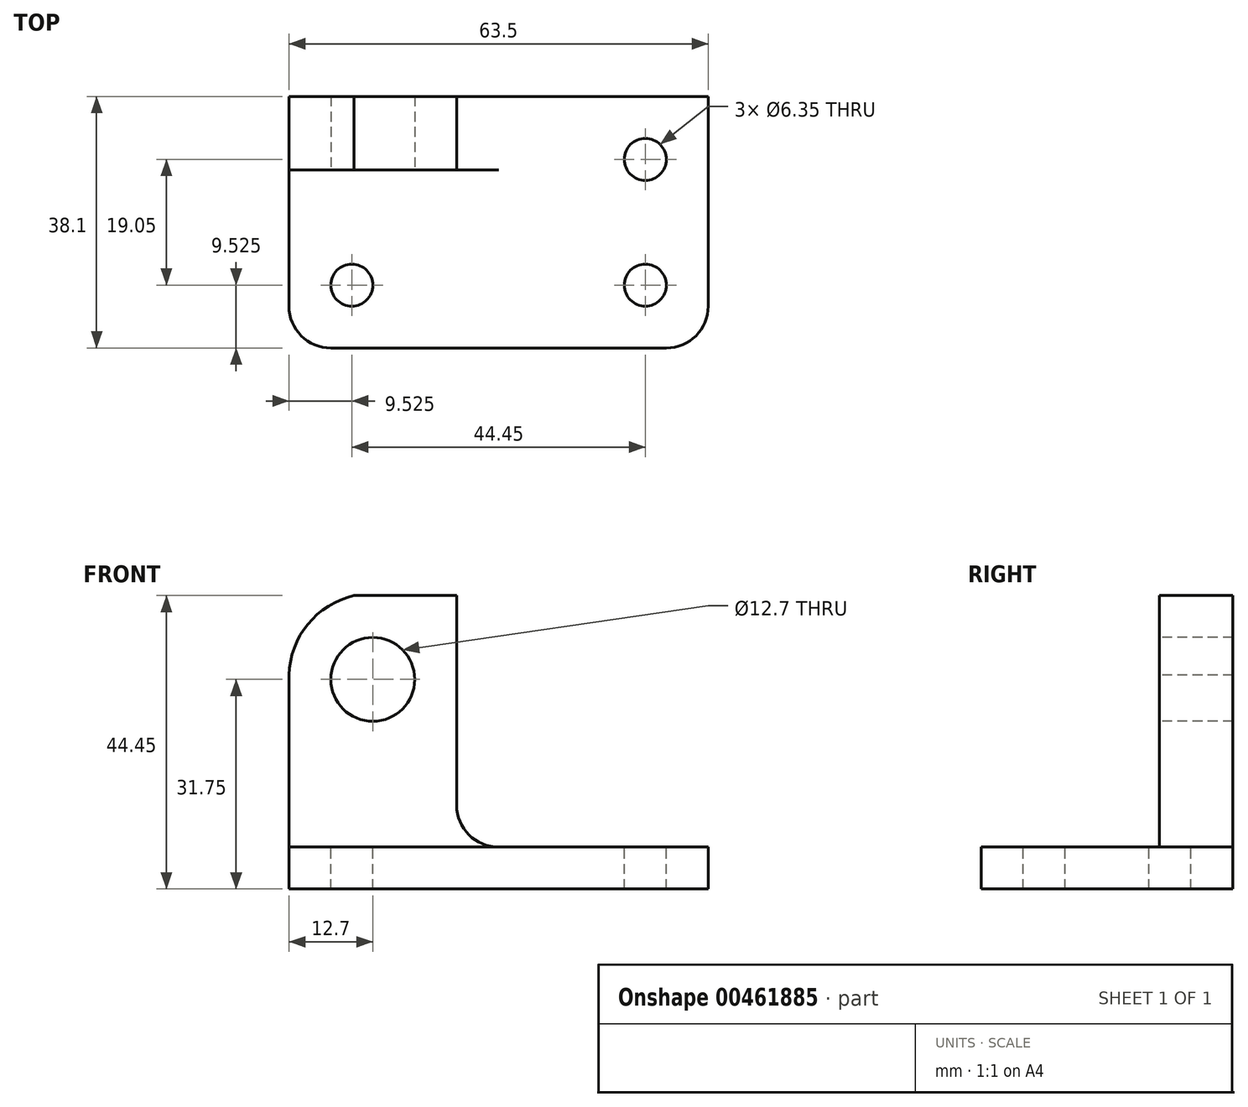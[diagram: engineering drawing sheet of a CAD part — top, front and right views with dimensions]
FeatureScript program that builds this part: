
annotation { "Feature Type Name" : "Feature", "Feature Type Description" : "" }
export const myFeature = defineFeature(function(context is Context, id is Id, definition is map)
    precondition{}
    {
        {
            var Q0;
            Q0=qCreatedBy(makeId("Right.planeOp"),FACE);
            var sketch = newSketch(context, id + "F0", { "sketchPlane" : qUnion([Q0])});
            skLineSegment(sketch, "E0", {"start": v(0, 0) * mm, "end": v(38.1, 0) * mm});
            skLineSegment(sketch, "E1", {"start": v(38.1, 0) * mm, "end": v(38.1, 44.45) * mm});
            skLineSegment(sketch, "E2", {"start": v(38.1, 44.45) * mm, "end": v(26.96, 44.45) * mm});
            skLineSegment(sketch, "E3", {"start": v(26.96, 44.45) * mm, "end": v(26.96, 6.35) * mm});
            skLineSegment(sketch, "E4", {"start": v(26.96, 6.35) * mm, "end": v(0, 6.35) * mm});
            skLineSegment(sketch, "E5", {"start": v(0, 6.35) * mm, "end": v(0, 0) * mm});
            skSolve(sketch);
        }
        {
            var Q0;
            Q0=makeQuery(id+"F0.imprint","IMPRINT",FACE,{"disambiguationData":[TD([[makeQuery(id+"F0.imprint","IMPRINT",EDGE,{"derivedFrom":sQuery(id+"F0.wireOp",EDGE,"E0")}),1.0]])]});
            extrude(context, id + "F1", {"entities" : qUnion([Q0]), "depth" : 63.5 * mm});
        }
        {
            var Q0;
            Q0=makeQuery(id+"F1.opExtrude","SWEPT_FACE",FACE,{"disambiguationData":[OSD([sQuery(id+"F0.wireOp",EDGE,"E3")])]});
            var sketch = newSketch(context, id + "F2", { "sketchPlane" : qUnion([Q0])});
            skLineSegment(sketch, "E6", {"start": v(25.4, 44.45) * mm, "end": v(25.4, 12.7) * mm});
            skLineSegment(sketch, "E7", {"start": v(31.75, 6.35) * mm, "end": v(63.5, 6.35) * mm});
            skPoint(sketch, "E8.visualSharp", {"position": v(25.4, 6.35) * mm});
            skArc(sketch, "E8.filletArc", {"start": v(25.4, 12.7) * mm, "mid": v(27.26, 8.2) * mm, "end": v(31.75, 6.35) * mm});
            skSolve(sketch);
        }
        {
            var Q0;
            {var subQ2=sQuery(id+"F2.wireOp",EDGE,"E6");Q0=makeQuery(id+"F2.imprint","IMPRINT",FACE,{"disambiguationData":[TD([[makeQuery(id+"F2.imprint","IMPRINT",EDGE,{"derivedFrom":subQ2}),1.0]])]});}
            extrude(context, id + "F3", {"entities" : qUnion([Q0]), "operationType" : NewBodyOperationType.REMOVE, "oppositeDirection" : true, "depth" : 12.7 * mm});
        }
        {
            var Q0;
            Q0=makeQuery(id+"F1.opExtrude","SWEPT_FACE",FACE,{"disambiguationData":[OSD([sQuery(id+"F0.wireOp",EDGE,"E3")])]});
            var sketch = newSketch(context, id + "F4", { "sketchPlane" : qUnion([Q0])});
            skCircle(sketch, "E9", {"center": v(12.7, 31.75) * mm, "radius": 6.35 * mm});
            skArc(sketch, "E10", {"start": v(25.4, 31.75) * mm, "mid": v(12.7, 44.77) * mm, "end": v(0, 31.75) * mm});
            skSolve(sketch);
        }
        {
            var Q0;
            {var subQ0=sQuery(id+"F4.wireOp",EDGE,"E10");var subQ1=makeQuery(id+"F3.boolean.opBoolean","COPY",EDGE,{"derivedFrom":makeQuery(id+"F3.opExtrude","CAP_EDGE",EDGE,{"disambiguationData":[OSD([sQuery(id+"F2.wireOp",EDGE,"E6")])],"isStart":true})});var subQ2=makeQuery(id+"F4.imprint","INTERSECT",VERTEX,{"disambiguationData":[OD(1.0)],"derivedFrom":[subQ1,subQ0]});Q0=makeQuery(id+"F4.imprint","IMPRINT",FACE,{"disambiguationData":[TD([[makeQuery(id+"F4.imprint","IMPRINT",EDGE,{"disambiguationData":[TD([[subQ2,-1.0]])],"derivedFrom":subQ0}),-1.0]])]});}
            var Q1;
            Q1=makeQuery(id+"F4.imprint","IMPRINT",FACE,{"disambiguationData":[TD([[makeQuery(id+"F4.imprint","IMPRINT",EDGE,{"derivedFrom":sQuery(id+"F4.wireOp",EDGE,"E9")}),1.0]])]});
            var Q2;
            {var subQ0=sQuery(id+"F4.wireOp",EDGE,"E10");var subQ1=sQuery(id+"F0.wireOp",EDGE,"E3");var subQ4=makeQuery(id+"F1.opExtrude","CAP_EDGE",EDGE,{"disambiguationData":[OSD([subQ1])],"isStart":true});var subQ5=makeQuery(id+"F4.imprint","INTERSECT",VERTEX,{"disambiguationData":[OD(1.0)],"derivedFrom":[subQ4,subQ0]});Q2=makeQuery(id+"F4.imprint","IMPRINT",FACE,{"disambiguationData":[TD([[makeQuery(id+"F4.imprint","IMPRINT",EDGE,{"disambiguationData":[TD([[subQ5,1.0]])],"derivedFrom":subQ0}),-1.0]])]});}
            extrude(context, id + "F5", {"entities" : qUnion([Q0, Q1, Q2]), "operationType" : NewBodyOperationType.REMOVE, "oppositeDirection" : true, "depth" : 12.7 * mm});
        }
        {
            var Q0;
            Q0=makeQuery(id+"F3.boolean.opBoolean","MERGE",FACE,{"derivedFrom":[makeQuery(id+"F1.opExtrude","SWEPT_FACE",FACE,{"disambiguationData":[OSD([sQuery(id+"F0.wireOp",EDGE,"E4")])]}),makeQuery(id+"F3.opExtrude","SWEPT_FACE",FACE,{"disambiguationData":[OSD([sQuery(id+"F2.wireOp",EDGE,"E7")])]})]});
            var sketch = newSketch(context, id + "F6", { "sketchPlane" : qUnion([Q0])});
            skCircle(sketch, "E11", {"center": v(53.98, 9.53) * mm, "radius": 3.18 * mm});
            skCircle(sketch, "E12", {"center": v(9.53, 9.53) * mm, "radius": 3.17 * mm});
            skCircle(sketch, "E13", {"center": v(53.97, 28.58) * mm, "radius": 3.18 * mm});
            skLineSegment(sketch, "E14", {"start": v(0, 26.96) * mm, "end": v(0, 6.35) * mm});
            skLineSegment(sketch, "E15", {"start": v(6.35, 0) * mm, "end": v(57.15, 0) * mm});
            skPoint(sketch, "E16.visualSharp", {"position": v(0, 0) * mm});
            skArc(sketch, "E16.filletArc", {"start": v(0, 6.35) * mm, "mid": v(1.86, 1.86) * mm, "end": v(6.35, 0) * mm});
            skLineSegment(sketch, "E17", {"start": v(63.5, 6.35) * mm, "end": v(63.5, 38.1) * mm});
            skPoint(sketch, "E18.visualSharp", {"position": v(63.5, 0) * mm});
            skArc(sketch, "E18.filletArc", {"start": v(57.15, 0) * mm, "mid": v(61.64, 1.86) * mm, "end": v(63.5, 6.35) * mm});
            skSolve(sketch);
        }
        {
            var Q0;
            Q0=makeQuery(id+"F6.imprint","IMPRINT",FACE,{"disambiguationData":[TD([[makeQuery(id+"F6.imprint","IMPRINT",EDGE,{"derivedFrom":sQuery(id+"F6.wireOp",EDGE,"E11")}),1.0]])]});
            var Q1;
            {var subQ0=sQuery(id+"F6.wireOp",EDGE,"E18.filletArc");Q1=makeQuery(id+"F6.imprint","IMPRINT",FACE,{"disambiguationData":[TD([[makeQuery(id+"F6.imprint","IMPRINT",EDGE,{"derivedFrom":subQ0}),-1.0]])]});}
            var Q2;
            {var subQ0=sQuery(id+"F6.wireOp",EDGE,"E16.filletArc");Q2=makeQuery(id+"F6.imprint","IMPRINT",FACE,{"disambiguationData":[TD([[makeQuery(id+"F6.imprint","IMPRINT",EDGE,{"derivedFrom":subQ0}),-1.0]])]});}
            var Q3;
            Q3=makeQuery(id+"F6.imprint","IMPRINT",FACE,{"disambiguationData":[TD([[makeQuery(id+"F6.imprint","IMPRINT",EDGE,{"derivedFrom":sQuery(id+"F6.wireOp",EDGE,"E12")}),1.0]])]});
            var Q4;
            Q4=makeQuery(id+"F6.imprint","IMPRINT",FACE,{"disambiguationData":[TD([[makeQuery(id+"F6.imprint","IMPRINT",EDGE,{"derivedFrom":sQuery(id+"F6.wireOp",EDGE,"E13")}),1.0]])]});
            extrude(context, id + "F7", {"entities" : qUnion([Q0, Q1, Q2, Q3, Q4]), "operationType" : NewBodyOperationType.REMOVE, "oppositeDirection" : true, "depth" : 6.35 * mm});
        }
    });
